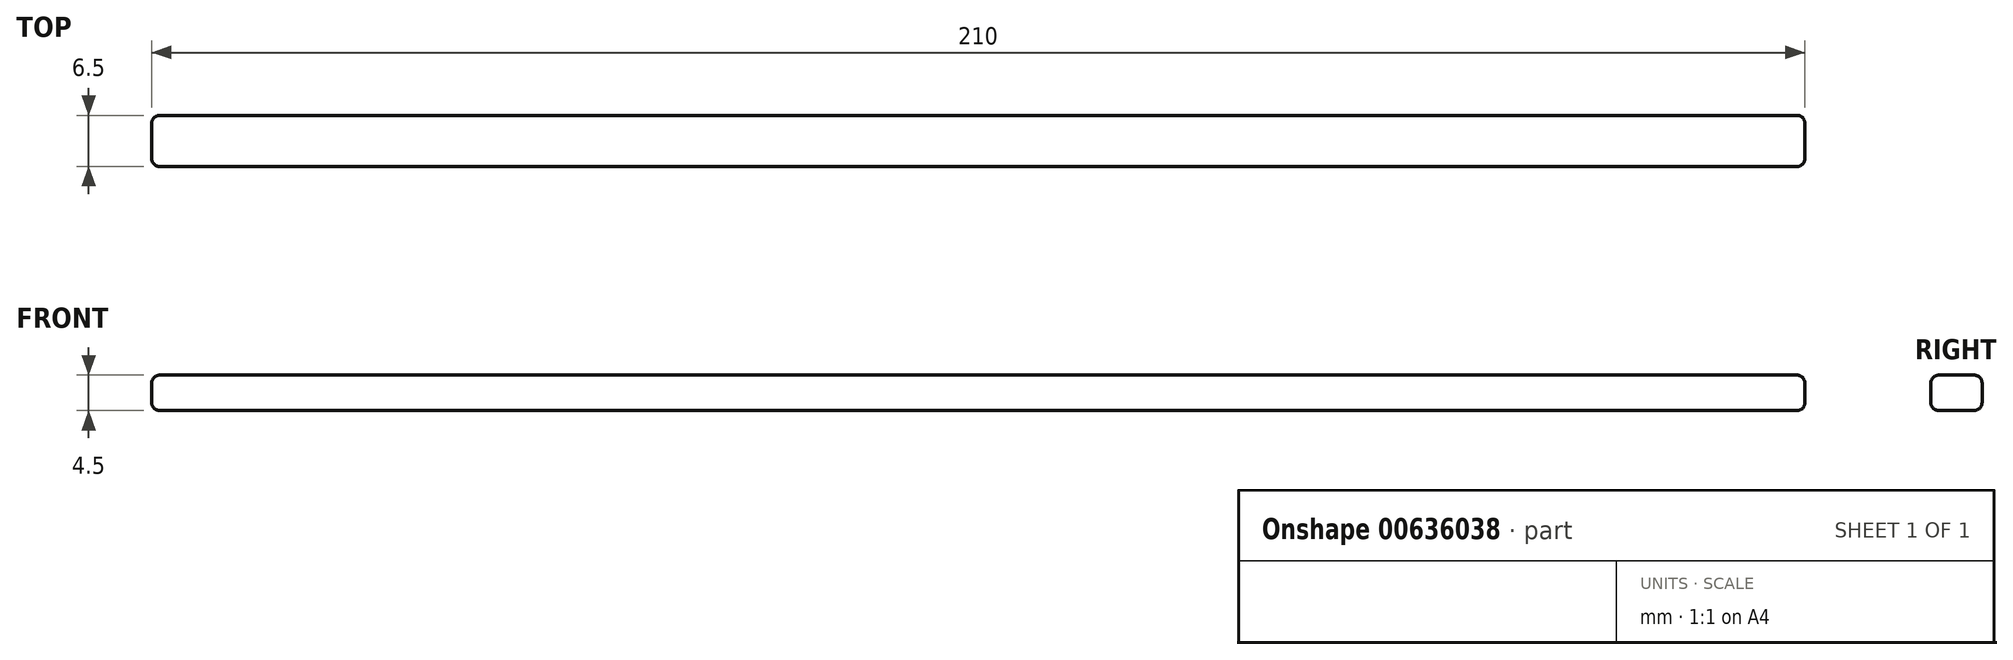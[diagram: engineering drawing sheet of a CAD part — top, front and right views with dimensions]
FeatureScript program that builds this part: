
annotation { "Feature Type Name" : "Feature", "Feature Type Description" : "" }
export const myFeature = defineFeature(function(context is Context, id is Id, definition is map)
    precondition{}
    {
        {
            var Q0;
            Q0=qCreatedBy(makeId("Top.planeOp"),FACE);
            var sketch = newSketch(context, id + "F0", { "sketchPlane" : qUnion([Q0])});
            skLineSegment(sketch, "E0.bottom", {"start": v(1, 0) * mm, "end": v(209, 0) * mm});
            skLineSegment(sketch, "E0.top", {"start": v(1, 6.5) * mm, "end": v(209, 6.5) * mm});
            skLineSegment(sketch, "E0.left", {"start": v(0, 1) * mm, "end": v(0, 5.5) * mm});
            skLineSegment(sketch, "E0.right", {"start": v(210, 1) * mm, "end": v(210, 5.5) * mm});
            skPoint(sketch, "E1.visualSharp", {"position": v(0, 6.5) * mm});
            skArc(sketch, "E1.filletArc", {"start": v(1, 6.5) * mm, "mid": v(0.3, 6.2) * mm, "end": v(0, 5.5) * mm});
            skPoint(sketch, "E2.visualSharp", {"position": v(0, 0) * mm});
            skArc(sketch, "E2.filletArc", {"start": v(0, 1) * mm, "mid": v(0.3, 0.3) * mm, "end": v(1, 0) * mm});
            skPoint(sketch, "E3.visualSharp", {"position": v(210, 0) * mm});
            skArc(sketch, "E3.filletArc", {"start": v(209, 0) * mm, "mid": v(209.7, 0.3) * mm, "end": v(210, 1) * mm});
            skPoint(sketch, "E4.visualSharp", {"position": v(210, 6.5) * mm});
            skArc(sketch, "E4.filletArc", {"start": v(210, 5.5) * mm, "mid": v(209.7, 6.2) * mm, "end": v(209, 6.5) * mm});
            skSolve(sketch);
        }
        {
            var Q0;
            Q0=qSketchRegion(id+"F0",true);
            extrude(context, id + "F1", {"entities" : qUnion([Q0]), "depth" : 4.5 * mm, "offsetDistance" : 25 * mm});
        }
        {
            var Q0;
            Q0=makeQuery(id+"F1.opExtrude","CAP_EDGE",EDGE,{"disambiguationData":[OSD([sQuery(id+"F0.wireOp",EDGE,"E0.left")])],"isStart":false});
            var Q1;
            Q1=makeQuery(id+"F1.opExtrude","CAP_EDGE",EDGE,{"disambiguationData":[OSD([sQuery(id+"F0.wireOp",EDGE,"E0.left")])],"isStart":true});
            fillet(context, id + "F2", {"entities" : qUnion([Q0, Q1]), "radius" : 1 * mm, "tangentPropagation" : true, "allowEdgeOverflow" : false});
        }
    });
